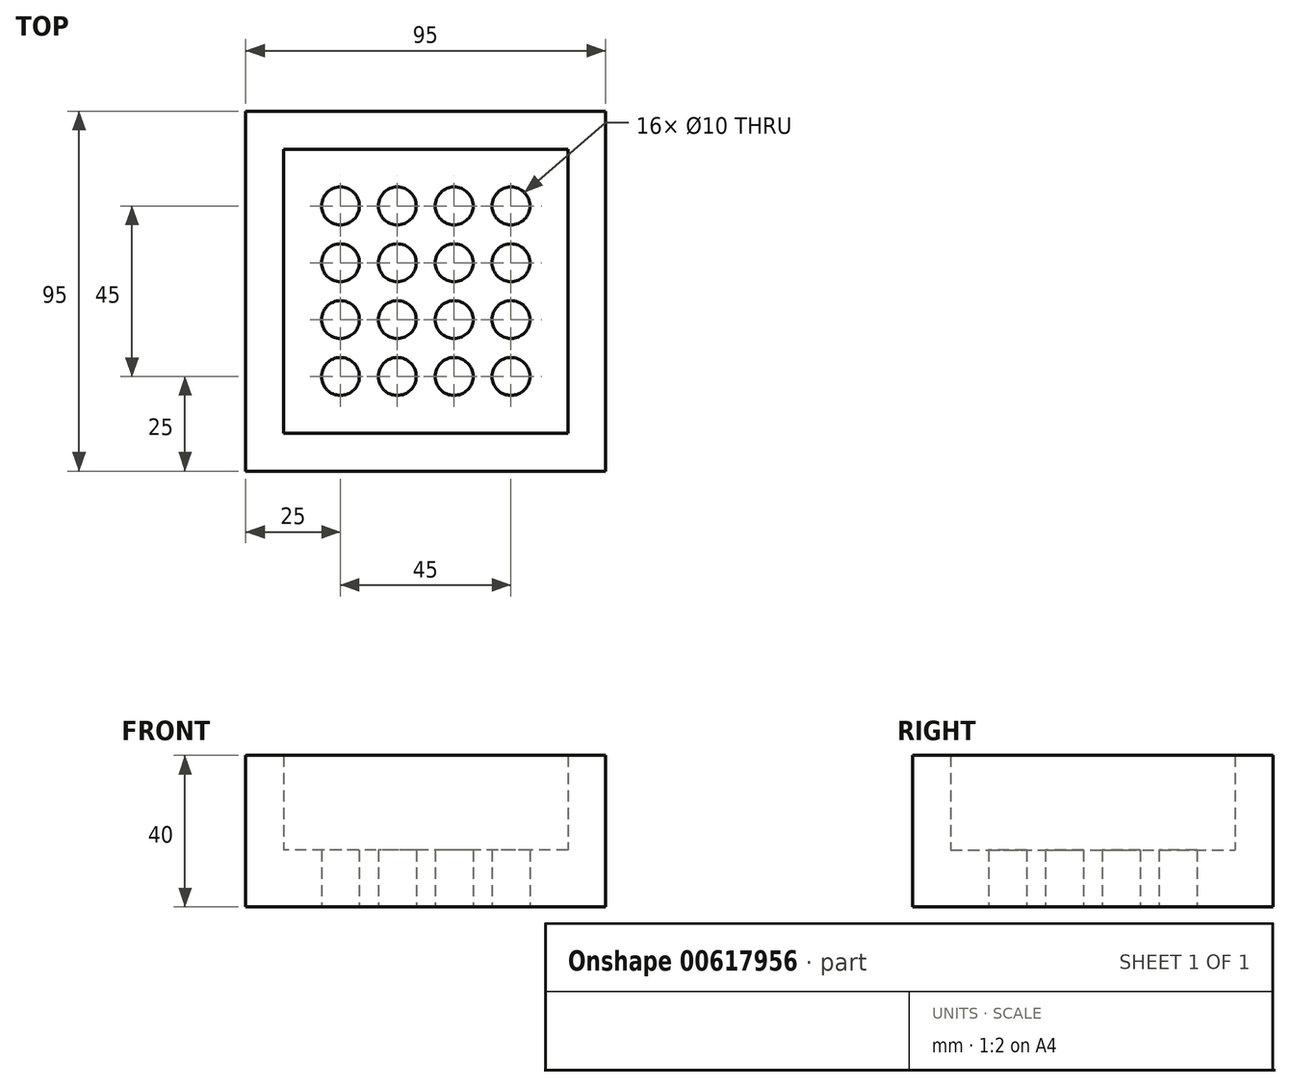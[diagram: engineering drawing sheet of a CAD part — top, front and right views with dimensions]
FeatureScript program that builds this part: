
annotation { "Feature Type Name" : "Feature", "Feature Type Description" : "" }
export const myFeature = defineFeature(function(context is Context, id is Id, definition is map)
    precondition{}
    {
        {
            var Q0;
            Q0=qCreatedBy(makeId("Top.planeOp"),FACE);
            var sketch = newSketch(context, id + "F0", { "sketchPlane" : qUnion([Q0])});
            skCircle(sketch, "E0", {"center": v(25, 25) * mm, "radius": 5 * mm});
            skCircle(sketch, "E1.0.1.0", {"center": v(25, 40) * mm, "radius": 5 * mm});
            skCircle(sketch, "E1.0.2.0", {"center": v(25, 55) * mm, "radius": 5 * mm});
            skCircle(sketch, "E1.0.3.0", {"center": v(25, 70) * mm, "radius": 5 * mm});
            skCircle(sketch, "E1.1.0.0", {"center": v(40, 25) * mm, "radius": 5 * mm});
            skCircle(sketch, "E1.1.1.0", {"center": v(40, 40) * mm, "radius": 5 * mm});
            skCircle(sketch, "E1.1.2.0", {"center": v(40, 55) * mm, "radius": 5 * mm});
            skCircle(sketch, "E1.1.3.0", {"center": v(40, 70) * mm, "radius": 5 * mm});
            skCircle(sketch, "E1.2.0.0", {"center": v(55, 25) * mm, "radius": 5 * mm});
            skCircle(sketch, "E1.2.1.0", {"center": v(55, 40) * mm, "radius": 5 * mm});
            skCircle(sketch, "E1.2.2.0", {"center": v(55, 55) * mm, "radius": 5 * mm});
            skCircle(sketch, "E1.2.3.0", {"center": v(55, 70) * mm, "radius": 5 * mm});
            skCircle(sketch, "E1.3.0.0", {"center": v(70, 25) * mm, "radius": 5 * mm});
            skCircle(sketch, "E1.3.1.0", {"center": v(70, 40) * mm, "radius": 5 * mm});
            skCircle(sketch, "E1.3.2.0", {"center": v(70, 55) * mm, "radius": 5 * mm});
            skCircle(sketch, "E1.3.3.0", {"center": v(70, 70) * mm, "radius": 5 * mm});
            skLineSegment(sketch, "E1.direction1", {"start": v(25, 25) * mm, "end": v(40, 25) * mm, "construction": true});
            skLineSegment(sketch, "E1.direction2", {"start": v(25, 25) * mm, "end": v(25, 40) * mm, "construction": true});
            skLineSegment(sketch, "E2.bottom", {"start": v(0, 0) * mm, "end": v(95, 0) * mm});
            skLineSegment(sketch, "E2.top", {"start": v(0, 95) * mm, "end": v(95, 95) * mm});
            skLineSegment(sketch, "E2.left", {"start": v(0, 0) * mm, "end": v(0, 95) * mm});
            skLineSegment(sketch, "E2.right", {"start": v(95, 0) * mm, "end": v(95, 95) * mm});
            skSolve(sketch);
        }
        {
            var Q0;
            Q0 = qSketchRegion(id + "F0", true);
            extrude(context, id + "F1", {"entities" : qUnion([Q0]), "depth" : 15 * mm, "offsetDistance" : 25 * mm});
        }
        {
            var Q0;
            Q0=makeQuery(id+"F1.opExtrude","CAP_FACE",FACE,{"disambiguationData":[OSD([sQuery(id+"F0.wireOp",EDGE,"E0"),sQuery(id+"F0.wireOp",EDGE,"E1.0.1.0"),sQuery(id+"F0.wireOp",EDGE,"E1.0.2.0"),sQuery(id+"F0.wireOp",EDGE,"E1.0.3.0"),sQuery(id+"F0.wireOp",EDGE,"E1.1.0.0"),sQuery(id+"F0.wireOp",EDGE,"E1.1.1.0"),sQuery(id+"F0.wireOp",EDGE,"E1.1.2.0"),sQuery(id+"F0.wireOp",EDGE,"E1.1.3.0"),sQuery(id+"F0.wireOp",EDGE,"E1.2.0.0"),sQuery(id+"F0.wireOp",EDGE,"E1.2.1.0"),sQuery(id+"F0.wireOp",EDGE,"E1.2.2.0"),sQuery(id+"F0.wireOp",EDGE,"E1.2.3.0"),sQuery(id+"F0.wireOp",EDGE,"E1.3.0.0"),sQuery(id+"F0.wireOp",EDGE,"E1.3.1.0"),sQuery(id+"F0.wireOp",EDGE,"E1.3.2.0"),sQuery(id+"F0.wireOp",EDGE,"E1.3.3.0"),sQuery(id+"F0.wireOp",EDGE,"E2.bottom"),sQuery(id+"F0.wireOp",EDGE,"E2.top"),sQuery(id+"F0.wireOp",EDGE,"E2.left"),sQuery(id+"F0.wireOp",EDGE,"E2.right")])],"isStart":false});
            var sketch = newSketch(context, id + "F2", { "sketchPlane" : qUnion([Q0])});
            skLineSegment(sketch, "E3.0", {"start": v(85, 85) * mm, "end": v(10, 85) * mm});
            skLineSegment(sketch, "E3.1", {"start": v(85, 10) * mm, "end": v(85, 85) * mm});
            skLineSegment(sketch, "E3.2", {"start": v(10, 10) * mm, "end": v(85, 10) * mm});
            skLineSegment(sketch, "E3.3", {"start": v(10, 85) * mm, "end": v(10, 10) * mm});
            skSolve(sketch);
        }
        {
            var Q0;
            Q0=makeQuery(id+"F2.imprint","IMPRINT",FACE,{"disambiguationData":[TD([[makeQuery(id+"F2.imprint","IMPRINT",EDGE,{"derivedFrom":sQuery(id+"F2.wireOp",EDGE,"E3.0")}),-1.0]])]});
            extrude(context, id + "F3", {"entities" : qUnion([Q0]), "operationType" : NewBodyOperationType.ADD, "depth" : 25 * mm, "offsetDistance" : 25 * mm});
        }
    });
